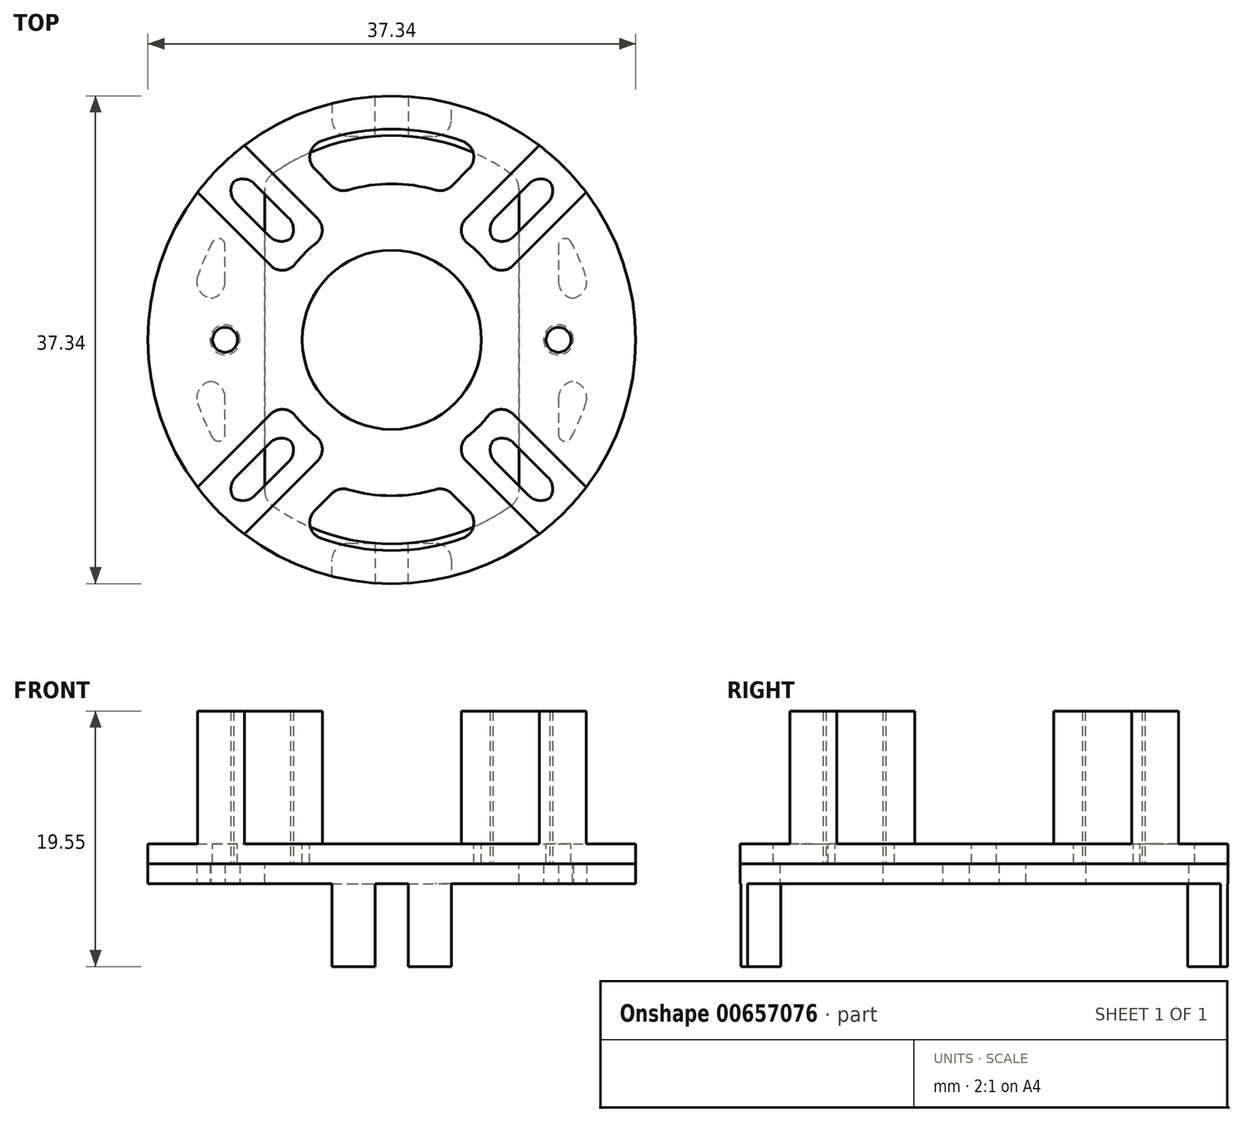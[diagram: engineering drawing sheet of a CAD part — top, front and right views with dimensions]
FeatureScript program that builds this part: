
annotation { "Feature Type Name" : "Feature", "Feature Type Description" : "" }
export const myFeature = defineFeature(function(context is Context, id is Id, definition is map)
    precondition{}
    {
        {
            var Q0;
            Q0=qCreatedBy(makeId("Top.planeOp"),FACE);
            var sketch = newSketch(context, id + "F0", { "sketchPlane" : qUnion([Q0])});
            skCircle(sketch, "E0", {"center": v(0, 0) * mm, "radius": 18.67 * mm});
            skSolve(sketch);
        }
        {
            var Q0;
            Q0=qSketchRegion(id+"F0",true);
            extrude(context, id + "F1", {"entities" : qUnion([Q0]), "depth" : 1.52 * mm, "offsetDistance" : 25.4 * mm});
        }
        {
            var Q0;
            Q0=makeQuery(id+"F1.opExtrude","CAP_FACE",FACE,{"disambiguationData":[OSD([sQuery(id+"F0.wireOp",EDGE,"E0")])],"isStart":false});
            var sketch = newSketch(context, id + "F2", { "sketchPlane" : qUnion([Q0])});
            skArc(sketch, "E1", {"start": v(-8.2, 4.6) * mm, "mid": v(-9.4, 0) * mm, "end": v(-8.2, -4.6) * mm, "construction": true});
            skArc(sketch, "E2", {"start": v(-4.6, 8.2) * mm, "mid": v(-6.65, 6.65) * mm, "end": v(-8.2, 4.6) * mm});
            skArc(sketch, "E3", {"start": v(4.6, 8.2) * mm, "mid": v(0, 9.4) * mm, "end": v(-4.6, 8.2) * mm, "construction": true});
            skArc(sketch, "E4", {"start": v(8.2, 4.6) * mm, "mid": v(6.65, 6.65) * mm, "end": v(4.6, 8.2) * mm});
            skArc(sketch, "E5", {"start": v(8.2, -4.6) * mm, "mid": v(9.4, 0) * mm, "end": v(8.2, 4.6) * mm, "construction": true});
            skArc(sketch, "E6", {"start": v(4.6, -8.2) * mm, "mid": v(6.65, -6.65) * mm, "end": v(8.2, -4.6) * mm});
            skArc(sketch, "E7", {"start": v(-4.6, -8.2) * mm, "mid": v(0, -9.4) * mm, "end": v(4.6, -8.2) * mm, "construction": true});
            skArc(sketch, "E8", {"start": v(-8.2, -4.6) * mm, "mid": v(-6.65, -6.65) * mm, "end": v(-4.6, -8.2) * mm});
            skArc(sketch, "E9", {"start": v(-14.87, -11.28) * mm, "mid": v(-13.2, -13.2) * mm, "end": v(-11.28, -14.87) * mm});
            skArc(sketch, "E10", {"start": v(-14.87, 11.28) * mm, "mid": v(-18.67, 0) * mm, "end": v(-14.87, -11.28) * mm, "construction": true});
            skArc(sketch, "E11", {"start": v(-11.28, 14.87) * mm, "mid": v(-13.2, 13.2) * mm, "end": v(-14.87, 11.28) * mm});
            skArc(sketch, "E12", {"start": v(11.28, 14.87) * mm, "mid": v(0, 18.67) * mm, "end": v(-11.28, 14.87) * mm, "construction": true});
            skArc(sketch, "E13", {"start": v(14.87, 11.28) * mm, "mid": v(13.2, 13.2) * mm, "end": v(11.28, 14.87) * mm});
            skArc(sketch, "E14", {"start": v(14.87, -11.28) * mm, "mid": v(18.67, 0) * mm, "end": v(14.87, 11.28) * mm, "construction": true});
            skArc(sketch, "E15", {"start": v(11.28, -14.87) * mm, "mid": v(13.2, -13.2) * mm, "end": v(14.87, -11.28) * mm});
            skArc(sketch, "E16", {"start": v(-11.28, -14.87) * mm, "mid": v(0, -18.67) * mm, "end": v(11.28, -14.87) * mm, "construction": true});
            skLineSegment(sketch, "E17", {"start": v(-14.87, 11.28) * mm, "end": v(-8.2, 4.6) * mm});
            skLineSegment(sketch, "E18", {"start": v(-4.6, 8.2) * mm, "end": v(-11.28, 14.87) * mm});
            skLineSegment(sketch, "E19", {"start": v(4.6, 8.2) * mm, "end": v(11.28, 14.87) * mm});
            skLineSegment(sketch, "E20", {"start": v(8.2, 4.6) * mm, "end": v(14.87, 11.28) * mm});
            skLineSegment(sketch, "E21", {"start": v(4.6, -8.2) * mm, "end": v(11.28, -14.87) * mm});
            skLineSegment(sketch, "E22", {"start": v(8.2, -4.6) * mm, "end": v(14.87, -11.28) * mm});
            skLineSegment(sketch, "E23", {"start": v(-11.28, -14.87) * mm, "end": v(-4.6, -8.2) * mm});
            skLineSegment(sketch, "E24", {"start": v(-14.87, -11.28) * mm, "end": v(-8.2, -4.6) * mm});
            skLineSegment(sketch, "E25", {"start": v(8.2, 4.6) * mm, "end": v(0, 4.6) * mm, "construction": true});
            skLineSegment(sketch, "E26", {"start": v(4.6, 8.2) * mm, "end": v(4.6, 0) * mm, "construction": true});
            skSolve(sketch);
        }
        {
            var Q0;
            Q0=qSketchRegion(id+"F2",true);
            extrude(context, id + "F3", {"entities" : qUnion([Q0]), "operationType" : NewBodyOperationType.ADD, "depth" : 10.16 * mm, "offsetDistance" : 25.4 * mm});
        }
        {
            var Q0;
            Q0=makeQuery(id+"F1.opExtrude","CAP_FACE",FACE,{"disambiguationData":[OSD([sQuery(id+"F0.wireOp",EDGE,"E0")])],"isStart":false});
            var sketch = newSketch(context, id + "F4", { "sketchPlane" : qUnion([Q0])});
            skCircle(sketch, "E27", {"center": v(0, 0) * mm, "radius": 6.86 * mm});
            skArc(sketch, "E28", {"start": v(-14.42, 7.23) * mm, "mid": v(-16.13, 0) * mm, "end": v(-14.42, -7.23) * mm, "construction": true});
            skArc(sketch, "E29", {"start": v(-14.42, -7.23) * mm, "mid": v(-11.4, -11.4) * mm, "end": v(-7.23, -14.42) * mm, "construction": true});
            skArc(sketch, "E30", {"start": v(-11.23, -4.05) * mm, "mid": v(-8.44, -8.44) * mm, "end": v(-4.05, -11.23) * mm, "construction": true});
            skArc(sketch, "E31", {"start": v(-11.23, 4.05) * mm, "mid": v(-11.94, 0) * mm, "end": v(-11.23, -4.05) * mm, "construction": true});
            skArc(sketch, "E32", {"start": v(-7.23, 14.42) * mm, "mid": v(-11.4, 11.4) * mm, "end": v(-14.42, 7.23) * mm, "construction": true});
            skArc(sketch, "E33", {"start": v(-4.05, 11.23) * mm, "mid": v(-8.44, 8.44) * mm, "end": v(-11.23, 4.05) * mm, "construction": true});
            skArc(sketch, "E34", {"start": v(4.05, 11.23) * mm, "mid": v(0, 11.94) * mm, "end": v(-4.05, 11.23) * mm});
            skArc(sketch, "E35", {"start": v(7.23, 14.42) * mm, "mid": v(0, 16.13) * mm, "end": v(-7.23, 14.42) * mm});
            skArc(sketch, "E36", {"start": v(14.42, 7.23) * mm, "mid": v(11.4, 11.4) * mm, "end": v(7.23, 14.42) * mm, "construction": true});
            skArc(sketch, "E37", {"start": v(11.23, 4.05) * mm, "mid": v(8.44, 8.44) * mm, "end": v(4.05, 11.23) * mm, "construction": true});
            skArc(sketch, "E38", {"start": v(11.23, -4.05) * mm, "mid": v(11.94, 0) * mm, "end": v(11.23, 4.05) * mm, "construction": true});
            skArc(sketch, "E39", {"start": v(14.42, -7.23) * mm, "mid": v(16.13, 0) * mm, "end": v(14.42, 7.23) * mm, "construction": true});
            skArc(sketch, "E40", {"start": v(7.23, -14.42) * mm, "mid": v(11.4, -11.4) * mm, "end": v(14.42, -7.23) * mm, "construction": true});
            skArc(sketch, "E41", {"start": v(4.05, -11.23) * mm, "mid": v(8.44, -8.44) * mm, "end": v(11.23, -4.05) * mm, "construction": true});
            skArc(sketch, "E42", {"start": v(-4.05, -11.23) * mm, "mid": v(0, -11.94) * mm, "end": v(4.05, -11.23) * mm});
            skArc(sketch, "E43", {"start": v(-7.23, -14.42) * mm, "mid": v(0, -16.13) * mm, "end": v(7.23, -14.42) * mm});
            skLineSegment(sketch, "E44", {"start": v(-14.42, -7.23) * mm, "end": v(-11.23, -4.05) * mm, "construction": true});
            skLineSegment(sketch, "E45", {"start": v(-14.42, 7.23) * mm, "end": v(-11.23, 4.05) * mm, "construction": true});
            skLineSegment(sketch, "E46", {"start": v(-7.23, 14.42) * mm, "end": v(-4.05, 11.23) * mm});
            skLineSegment(sketch, "E47", {"start": v(4.05, 11.23) * mm, "end": v(7.23, 14.42) * mm});
            skLineSegment(sketch, "E48", {"start": v(11.23, 4.05) * mm, "end": v(14.42, 7.23) * mm, "construction": true});
            skLineSegment(sketch, "E49", {"start": v(11.23, -4.05) * mm, "end": v(14.42, -7.23) * mm, "construction": true});
            skLineSegment(sketch, "E50", {"start": v(4.05, -11.23) * mm, "end": v(7.23, -14.42) * mm});
            skLineSegment(sketch, "E51", {"start": v(-7.23, -14.42) * mm, "end": v(-4.05, -11.23) * mm});
            skSolve(sketch);
        }
        {
            var Q0;
            Q0=qSketchRegion(id+"F4",true);
            var Q1;
            Q1=makeQuery(id+"F1.opExtrude","SWEPT_BODY",BODY,{"disambiguationData":[OSD([sQuery(id+"F0.wireOp",EDGE,"E0")])]});
            extrude(context, id + "F5", {"entities" : qUnion([Q0]), "operationType" : NewBodyOperationType.REMOVE, "endBound" : BoundingType.UP_TO_BODY, "oppositeDirection" : true, "depth" : 25.4 * mm, "endBoundEntityBody" : qUnion([Q1]), "offsetDistance" : 25.4 * mm});
        }
        {
            var Q0;
            Q0=makeQuery(id+"F5.boolean.opBoolean","COPY",EDGE,{"derivedFrom":makeQuery(id+"F5.opExtrude","SWEPT_EDGE",EDGE,{"disambiguationData":[OSD([sQuery(id+"F4.wireOp",EDGE,"E28"),sQuery(id+"F4.wireOp",EDGE,"E45")])]})});
            var Q1;
            Q1=makeQuery(id+"F5.boolean.opBoolean","COPY",EDGE,{"derivedFrom":makeQuery(id+"F5.opExtrude","SWEPT_EDGE",EDGE,{"disambiguationData":[OSD([sQuery(id+"F4.wireOp",EDGE,"E31"),sQuery(id+"F4.wireOp",EDGE,"E45")])]})});
            var Q2;
            Q2=makeQuery(id+"F5.boolean.opBoolean","COPY",EDGE,{"derivedFrom":makeQuery(id+"F5.opExtrude","SWEPT_EDGE",EDGE,{"disambiguationData":[OSD([sQuery(id+"F4.wireOp",EDGE,"E31"),sQuery(id+"F4.wireOp",EDGE,"E44")])]})});
            var Q3;
            Q3=makeQuery(id+"F5.boolean.opBoolean","COPY",EDGE,{"derivedFrom":makeQuery(id+"F5.opExtrude","SWEPT_EDGE",EDGE,{"disambiguationData":[OSD([sQuery(id+"F4.wireOp",EDGE,"E28"),sQuery(id+"F4.wireOp",EDGE,"E44")])]})});
            var Q4;
            Q4=makeQuery(id+"F5.boolean.opBoolean","COPY",EDGE,{"derivedFrom":makeQuery(id+"F5.opExtrude","SWEPT_EDGE",EDGE,{"disambiguationData":[OSD([sQuery(id+"F4.wireOp",EDGE,"E34"),sQuery(id+"F4.wireOp",EDGE,"E46")])]})});
            var Q5;
            Q5=makeQuery(id+"F5.boolean.opBoolean","COPY",EDGE,{"derivedFrom":makeQuery(id+"F5.opExtrude","SWEPT_EDGE",EDGE,{"disambiguationData":[OSD([sQuery(id+"F4.wireOp",EDGE,"E34"),sQuery(id+"F4.wireOp",EDGE,"E47")])]})});
            var Q6;
            Q6=makeQuery(id+"F5.boolean.opBoolean","COPY",EDGE,{"derivedFrom":makeQuery(id+"F5.opExtrude","SWEPT_EDGE",EDGE,{"disambiguationData":[OSD([sQuery(id+"F4.wireOp",EDGE,"E35"),sQuery(id+"F4.wireOp",EDGE,"E46")])]})});
            var Q7;
            Q7=makeQuery(id+"F5.boolean.opBoolean","COPY",EDGE,{"derivedFrom":makeQuery(id+"F5.opExtrude","SWEPT_EDGE",EDGE,{"disambiguationData":[OSD([sQuery(id+"F4.wireOp",EDGE,"E35"),sQuery(id+"F4.wireOp",EDGE,"E47")])]})});
            var Q8;
            Q8=makeQuery(id+"F5.boolean.opBoolean","COPY",EDGE,{"derivedFrom":makeQuery(id+"F5.opExtrude","SWEPT_EDGE",EDGE,{"disambiguationData":[OSD([sQuery(id+"F4.wireOp",EDGE,"E42"),sQuery(id+"F4.wireOp",EDGE,"E50")])]})});
            var Q9;
            Q9=makeQuery(id+"F5.boolean.opBoolean","COPY",EDGE,{"derivedFrom":makeQuery(id+"F5.opExtrude","SWEPT_EDGE",EDGE,{"disambiguationData":[OSD([sQuery(id+"F4.wireOp",EDGE,"E42"),sQuery(id+"F4.wireOp",EDGE,"E51")])]})});
            var Q10;
            Q10=makeQuery(id+"F5.boolean.opBoolean","COPY",EDGE,{"derivedFrom":makeQuery(id+"F5.opExtrude","SWEPT_EDGE",EDGE,{"disambiguationData":[OSD([sQuery(id+"F4.wireOp",EDGE,"E39"),sQuery(id+"F4.wireOp",EDGE,"E48")])]})});
            var Q11;
            Q11=makeQuery(id+"F5.boolean.opBoolean","COPY",EDGE,{"derivedFrom":makeQuery(id+"F5.opExtrude","SWEPT_EDGE",EDGE,{"disambiguationData":[OSD([sQuery(id+"F4.wireOp",EDGE,"E43"),sQuery(id+"F4.wireOp",EDGE,"E50")])]})});
            var Q12;
            Q12=makeQuery(id+"F5.boolean.opBoolean","COPY",EDGE,{"derivedFrom":makeQuery(id+"F5.opExtrude","SWEPT_EDGE",EDGE,{"disambiguationData":[OSD([sQuery(id+"F4.wireOp",EDGE,"E43"),sQuery(id+"F4.wireOp",EDGE,"E51")])]})});
            var Q13;
            Q13=makeQuery(id+"F5.boolean.opBoolean","COPY",EDGE,{"derivedFrom":makeQuery(id+"F5.opExtrude","SWEPT_EDGE",EDGE,{"disambiguationData":[OSD([sQuery(id+"F4.wireOp",EDGE,"E38"),sQuery(id+"F4.wireOp",EDGE,"E48")])]})});
            var Q14;
            Q14=makeQuery(id+"F5.boolean.opBoolean","COPY",EDGE,{"derivedFrom":makeQuery(id+"F5.opExtrude","SWEPT_EDGE",EDGE,{"disambiguationData":[OSD([sQuery(id+"F4.wireOp",EDGE,"E38"),sQuery(id+"F4.wireOp",EDGE,"E49")])]})});
            var Q15;
            Q15=makeQuery(id+"F5.boolean.opBoolean","COPY",EDGE,{"derivedFrom":makeQuery(id+"F5.opExtrude","SWEPT_EDGE",EDGE,{"disambiguationData":[OSD([sQuery(id+"F4.wireOp",EDGE,"E39"),sQuery(id+"F4.wireOp",EDGE,"E49")])]})});
            var Q16;
            Q16=makeQuery(id+"F3.opExtrude","SWEPT_EDGE",EDGE,{"disambiguationData":[OSD([sQuery(id+"F2.wireOp",EDGE,"E8"),sQuery(id+"F2.wireOp",EDGE,"E23")])]});
            var Q17;
            Q17=makeQuery(id+"F3.opExtrude","SWEPT_EDGE",EDGE,{"disambiguationData":[OSD([sQuery(id+"F2.wireOp",EDGE,"E8"),sQuery(id+"F2.wireOp",EDGE,"E24")])]});
            var Q18;
            Q18=makeQuery(id+"F3.opExtrude","SWEPT_EDGE",EDGE,{"disambiguationData":[OSD([sQuery(id+"F2.wireOp",EDGE,"E2"),sQuery(id+"F2.wireOp",EDGE,"E17")])]});
            var Q19;
            Q19=makeQuery(id+"F3.opExtrude","SWEPT_EDGE",EDGE,{"disambiguationData":[OSD([sQuery(id+"F2.wireOp",EDGE,"E2"),sQuery(id+"F2.wireOp",EDGE,"E18")])]});
            var Q20;
            Q20=makeQuery(id+"F3.opExtrude","SWEPT_EDGE",EDGE,{"disambiguationData":[OSD([sQuery(id+"F2.wireOp",EDGE,"E6"),sQuery(id+"F2.wireOp",EDGE,"E22")])]});
            var Q21;
            Q21=makeQuery(id+"F3.opExtrude","SWEPT_EDGE",EDGE,{"disambiguationData":[OSD([sQuery(id+"F2.wireOp",EDGE,"E4"),sQuery(id+"F2.wireOp",EDGE,"E20")])]});
            var Q22;
            Q22=makeQuery(id+"F3.opExtrude","SWEPT_EDGE",EDGE,{"disambiguationData":[OSD([sQuery(id+"F2.wireOp",EDGE,"E4"),sQuery(id+"F2.wireOp",EDGE,"E19")])]});
            var Q23;
            Q23=makeQuery(id+"F3.opExtrude","SWEPT_EDGE",EDGE,{"disambiguationData":[OSD([sQuery(id+"F2.wireOp",EDGE,"E6"),sQuery(id+"F2.wireOp",EDGE,"E21")])]});
            fillet(context, id + "F6", {"entities" : qUnion([Q0, Q1, Q2, Q3, Q4, Q5, Q6, Q7, Q8, Q9, Q10, Q11, Q12, Q13, Q14, Q15, Q16, Q17, Q18, Q19, Q20, Q21, Q22, Q23]), "radius" : 1.27 * mm, "tangentPropagation" : true, "allowEdgeOverflow" : false});
        }
        {
            var Q0;
            Q0=makeQuery(id+"F3.opExtrude","CAP_FACE",FACE,{"disambiguationData":[OSD([sQuery(id+"F2.wireOp",EDGE,"E8"),sQuery(id+"F2.wireOp",EDGE,"E9"),sQuery(id+"F2.wireOp",EDGE,"E23"),sQuery(id+"F2.wireOp",EDGE,"E24")])],"isStart":false});
            var Q1;
            Q1=makeQuery(id+"F3.opExtrude","CAP_FACE",FACE,{"disambiguationData":[OSD([sQuery(id+"F2.wireOp",EDGE,"E2"),sQuery(id+"F2.wireOp",EDGE,"E11"),sQuery(id+"F2.wireOp",EDGE,"E17"),sQuery(id+"F2.wireOp",EDGE,"E18")])],"isStart":false});
            var Q2;
            Q2=makeQuery(id+"F3.opExtrude","CAP_FACE",FACE,{"disambiguationData":[OSD([sQuery(id+"F2.wireOp",EDGE,"E6"),sQuery(id+"F2.wireOp",EDGE,"E15"),sQuery(id+"F2.wireOp",EDGE,"E21"),sQuery(id+"F2.wireOp",EDGE,"E22")])],"isStart":false});
            var Q3;
            Q3=makeQuery(id+"F3.opExtrude","CAP_FACE",FACE,{"disambiguationData":[OSD([sQuery(id+"F2.wireOp",EDGE,"E4"),sQuery(id+"F2.wireOp",EDGE,"E13"),sQuery(id+"F2.wireOp",EDGE,"E19"),sQuery(id+"F2.wireOp",EDGE,"E20")])],"isStart":false});
            shell(context, id + "F7", {"entities" : qUnion([Q0, Q1, Q2, Q3]), "thickness" : 1.52 * mm});
        }
        {
            var Q0;
            Q0=makeQuery(id+"F7.opShell","OFFSET_FACE",FACE,{"disambiguationData":[OSD([sQuery(id+"F0.wireOp",EDGE,"E0")]),OD(3.0)]});
            var Q1;
            Q1=makeQuery(id+"F7.opShell","OFFSET_FACE",FACE,{"disambiguationData":[OSD([sQuery(id+"F0.wireOp",EDGE,"E0")]),OD(0.0)]});
            var Q2;
            Q2=makeQuery(id+"F7.opShell","OFFSET_FACE",FACE,{"disambiguationData":[OSD([sQuery(id+"F0.wireOp",EDGE,"E0")]),OD(2.0)]});
            var Q3;
            Q3=makeQuery(id+"F7.opShell","OFFSET_FACE",FACE,{"disambiguationData":[OSD([sQuery(id+"F0.wireOp",EDGE,"E0")]),OD(1.0)]});
            var Q4;
            Q4=makeQuery(id+"F1.opExtrude","CAP_FACE",FACE,{"disambiguationData":[OSD([sQuery(id+"F0.wireOp",EDGE,"E0")])],"isStart":true});
            extrude(context, id + "F8", {"entities" : qUnion([Q0, Q1, Q2, Q3]), "operationType" : NewBodyOperationType.REMOVE, "endBound" : BoundingType.UP_TO_SURFACE, "oppositeDirection" : true, "depth" : 25.4 * mm, "endBoundEntityFace" : qUnion([Q4]), "offsetDistance" : 25.4 * mm});
        }
        {
            var Q0;
            Q0=makeQuery(id+"F3.opExtrude","CAP_EDGE",EDGE,{"disambiguationData":[OSD([sQuery(id+"F2.wireOp",EDGE,"E4")])],"isStart":true});
            var Q1;
            Q1=makeQuery(id+"F3.opExtrude","CAP_EDGE",EDGE,{"disambiguationData":[OSD([sQuery(id+"F2.wireOp",EDGE,"E2")])],"isStart":true});
            var Q2;
            Q2=makeQuery(id+"F3.opExtrude","CAP_EDGE",EDGE,{"disambiguationData":[OSD([sQuery(id+"F2.wireOp",EDGE,"E8")])],"isStart":true});
            var Q3;
            Q3=makeQuery(id+"F3.opExtrude","CAP_EDGE",EDGE,{"disambiguationData":[OSD([sQuery(id+"F2.wireOp",EDGE,"E6")])],"isStart":true});
            var Q4;
            {var subQ0=sQuery(id+"F2.wireOp",EDGE,"E17");var subQ1=sQuery(id+"F2.wireOp",EDGE,"E2");Q4=makeQuery(id+"F8.boolean.opBoolean","MERGE",EDGE,{"derivedFrom":[makeQuery(id+"F7.opShell","OFFSET_EDGE",EDGE,{"disambiguationData":[OSD([subQ1,subQ0])]}),makeQuery(id+"F8.opExtrude","SWEPT_EDGE",EDGE,{"disambiguationData":[OSD([sQuery(id+"F0.wireOp",EDGE,"E0"),subQ1,subQ0])]})]});}
            var Q5;
            {var subQ0=sQuery(id+"F2.wireOp",EDGE,"E18");var subQ1=sQuery(id+"F2.wireOp",EDGE,"E2");Q5=makeQuery(id+"F8.boolean.opBoolean","MERGE",EDGE,{"derivedFrom":[makeQuery(id+"F7.opShell","OFFSET_EDGE",EDGE,{"disambiguationData":[OSD([subQ1,subQ0])]}),makeQuery(id+"F8.opExtrude","SWEPT_EDGE",EDGE,{"disambiguationData":[OSD([sQuery(id+"F0.wireOp",EDGE,"E0"),subQ1,subQ0])]})]});}
            var Q6;
            {var subQ0=sQuery(id+"F2.wireOp",EDGE,"E18");var subQ1=sQuery(id+"F2.wireOp",EDGE,"E11");var subQ2=sQuery(id+"F0.wireOp",EDGE,"E0");Q6=makeQuery(id+"F8.boolean.opBoolean","MERGE",EDGE,{"derivedFrom":[makeQuery(id+"F7.opShell","OFFSET_EDGE",EDGE,{"disambiguationData":[OSD([subQ2,subQ1,subQ0])]}),makeQuery(id+"F8.opExtrude","SWEPT_EDGE",EDGE,{"disambiguationData":[OSD([subQ2,sQuery(id+"F2.wireOp",EDGE,"E9"),subQ1,sQuery(id+"F2.wireOp",EDGE,"E13"),sQuery(id+"F2.wireOp",EDGE,"E15"),subQ0])]})]});}
            var Q7;
            {var subQ0=sQuery(id+"F2.wireOp",EDGE,"E17");var subQ1=sQuery(id+"F2.wireOp",EDGE,"E11");var subQ2=sQuery(id+"F0.wireOp",EDGE,"E0");Q7=makeQuery(id+"F8.boolean.opBoolean","MERGE",EDGE,{"derivedFrom":[makeQuery(id+"F7.opShell","OFFSET_EDGE",EDGE,{"disambiguationData":[OSD([subQ2,subQ1,subQ0])]}),makeQuery(id+"F8.opExtrude","SWEPT_EDGE",EDGE,{"disambiguationData":[OSD([subQ2,sQuery(id+"F2.wireOp",EDGE,"E9"),subQ1,sQuery(id+"F2.wireOp",EDGE,"E13"),sQuery(id+"F2.wireOp",EDGE,"E15"),subQ0])]})]});}
            var Q8;
            {var subQ0=sQuery(id+"F2.wireOp",EDGE,"E24");var subQ1=sQuery(id+"F2.wireOp",EDGE,"E8");Q8=makeQuery(id+"F8.boolean.opBoolean","MERGE",EDGE,{"derivedFrom":[makeQuery(id+"F7.opShell","OFFSET_EDGE",EDGE,{"disambiguationData":[OSD([subQ1,subQ0])]}),makeQuery(id+"F8.opExtrude","SWEPT_EDGE",EDGE,{"disambiguationData":[OSD([sQuery(id+"F0.wireOp",EDGE,"E0"),subQ1,subQ0])]})]});}
            var Q9;
            {var subQ0=sQuery(id+"F2.wireOp",EDGE,"E24");var subQ1=sQuery(id+"F2.wireOp",EDGE,"E9");var subQ2=sQuery(id+"F0.wireOp",EDGE,"E0");Q9=makeQuery(id+"F8.boolean.opBoolean","MERGE",EDGE,{"derivedFrom":[makeQuery(id+"F7.opShell","OFFSET_EDGE",EDGE,{"disambiguationData":[OSD([subQ2,subQ1,subQ0])]}),makeQuery(id+"F8.opExtrude","SWEPT_EDGE",EDGE,{"disambiguationData":[OSD([subQ2,subQ1,sQuery(id+"F2.wireOp",EDGE,"E11"),sQuery(id+"F2.wireOp",EDGE,"E13"),sQuery(id+"F2.wireOp",EDGE,"E15"),subQ0])]})]});}
            var Q10;
            {var subQ0=sQuery(id+"F2.wireOp",EDGE,"E23");var subQ1=sQuery(id+"F2.wireOp",EDGE,"E9");var subQ2=sQuery(id+"F0.wireOp",EDGE,"E0");Q10=makeQuery(id+"F8.boolean.opBoolean","MERGE",EDGE,{"derivedFrom":[makeQuery(id+"F7.opShell","OFFSET_EDGE",EDGE,{"disambiguationData":[OSD([subQ2,subQ1,subQ0])]}),makeQuery(id+"F8.opExtrude","SWEPT_EDGE",EDGE,{"disambiguationData":[OSD([subQ2,subQ1,sQuery(id+"F2.wireOp",EDGE,"E11"),sQuery(id+"F2.wireOp",EDGE,"E13"),sQuery(id+"F2.wireOp",EDGE,"E15"),subQ0])]})]});}
            var Q11;
            {var subQ0=sQuery(id+"F2.wireOp",EDGE,"E23");var subQ1=sQuery(id+"F2.wireOp",EDGE,"E8");Q11=makeQuery(id+"F8.boolean.opBoolean","MERGE",EDGE,{"derivedFrom":[makeQuery(id+"F7.opShell","OFFSET_EDGE",EDGE,{"disambiguationData":[OSD([subQ1,subQ0])]}),makeQuery(id+"F8.opExtrude","SWEPT_EDGE",EDGE,{"disambiguationData":[OSD([sQuery(id+"F0.wireOp",EDGE,"E0"),subQ1,subQ0])]})]});}
            var Q12;
            {var subQ0=sQuery(id+"F2.wireOp",EDGE,"E20");var subQ1=sQuery(id+"F2.wireOp",EDGE,"E13");var subQ2=sQuery(id+"F0.wireOp",EDGE,"E0");Q12=makeQuery(id+"F8.boolean.opBoolean","MERGE",EDGE,{"derivedFrom":[makeQuery(id+"F7.opShell","OFFSET_EDGE",EDGE,{"disambiguationData":[OSD([subQ2,subQ1,subQ0])]}),makeQuery(id+"F8.opExtrude","SWEPT_EDGE",EDGE,{"disambiguationData":[OSD([subQ2,sQuery(id+"F2.wireOp",EDGE,"E9"),sQuery(id+"F2.wireOp",EDGE,"E11"),subQ1,sQuery(id+"F2.wireOp",EDGE,"E15"),subQ0])]})]});}
            var Q13;
            {var subQ0=sQuery(id+"F2.wireOp",EDGE,"E22");var subQ1=sQuery(id+"F2.wireOp",EDGE,"E15");var subQ2=sQuery(id+"F0.wireOp",EDGE,"E0");Q13=makeQuery(id+"F8.boolean.opBoolean","MERGE",EDGE,{"derivedFrom":[makeQuery(id+"F7.opShell","OFFSET_EDGE",EDGE,{"disambiguationData":[OSD([subQ2,subQ1,subQ0])]}),makeQuery(id+"F8.opExtrude","SWEPT_EDGE",EDGE,{"disambiguationData":[OSD([subQ2,sQuery(id+"F2.wireOp",EDGE,"E9"),sQuery(id+"F2.wireOp",EDGE,"E11"),sQuery(id+"F2.wireOp",EDGE,"E13"),subQ1,subQ0])]})]});}
            var Q14;
            {var subQ0=sQuery(id+"F2.wireOp",EDGE,"E19");var subQ1=sQuery(id+"F2.wireOp",EDGE,"E4");Q14=makeQuery(id+"F8.boolean.opBoolean","MERGE",EDGE,{"derivedFrom":[makeQuery(id+"F7.opShell","OFFSET_EDGE",EDGE,{"disambiguationData":[OSD([subQ1,subQ0])]}),makeQuery(id+"F8.opExtrude","SWEPT_EDGE",EDGE,{"disambiguationData":[OSD([sQuery(id+"F0.wireOp",EDGE,"E0"),subQ1,subQ0])]})]});}
            var Q15;
            {var subQ0=sQuery(id+"F2.wireOp",EDGE,"E21");var subQ1=sQuery(id+"F2.wireOp",EDGE,"E6");Q15=makeQuery(id+"F8.boolean.opBoolean","MERGE",EDGE,{"derivedFrom":[makeQuery(id+"F7.opShell","OFFSET_EDGE",EDGE,{"disambiguationData":[OSD([subQ1,subQ0])]}),makeQuery(id+"F8.opExtrude","SWEPT_EDGE",EDGE,{"disambiguationData":[OSD([sQuery(id+"F0.wireOp",EDGE,"E0"),subQ1,subQ0])]})]});}
            var Q16;
            {var subQ0=sQuery(id+"F2.wireOp",EDGE,"E19");var subQ1=sQuery(id+"F2.wireOp",EDGE,"E13");var subQ2=sQuery(id+"F0.wireOp",EDGE,"E0");Q16=makeQuery(id+"F8.boolean.opBoolean","MERGE",EDGE,{"derivedFrom":[makeQuery(id+"F7.opShell","OFFSET_EDGE",EDGE,{"disambiguationData":[OSD([subQ2,subQ1,subQ0])]}),makeQuery(id+"F8.opExtrude","SWEPT_EDGE",EDGE,{"disambiguationData":[OSD([subQ2,sQuery(id+"F2.wireOp",EDGE,"E9"),sQuery(id+"F2.wireOp",EDGE,"E11"),subQ1,sQuery(id+"F2.wireOp",EDGE,"E15"),subQ0])]})]});}
            var Q17;
            {var subQ0=sQuery(id+"F2.wireOp",EDGE,"E22");var subQ1=sQuery(id+"F2.wireOp",EDGE,"E6");Q17=makeQuery(id+"F8.boolean.opBoolean","MERGE",EDGE,{"derivedFrom":[makeQuery(id+"F7.opShell","OFFSET_EDGE",EDGE,{"disambiguationData":[OSD([subQ1,subQ0])]}),makeQuery(id+"F8.opExtrude","SWEPT_EDGE",EDGE,{"disambiguationData":[OSD([sQuery(id+"F0.wireOp",EDGE,"E0"),subQ1,subQ0])]})]});}
            var Q18;
            {var subQ0=sQuery(id+"F2.wireOp",EDGE,"E21");var subQ1=sQuery(id+"F2.wireOp",EDGE,"E15");var subQ2=sQuery(id+"F0.wireOp",EDGE,"E0");Q18=makeQuery(id+"F8.boolean.opBoolean","MERGE",EDGE,{"derivedFrom":[makeQuery(id+"F7.opShell","OFFSET_EDGE",EDGE,{"disambiguationData":[OSD([subQ2,subQ1,subQ0])]}),makeQuery(id+"F8.opExtrude","SWEPT_EDGE",EDGE,{"disambiguationData":[OSD([subQ2,sQuery(id+"F2.wireOp",EDGE,"E9"),sQuery(id+"F2.wireOp",EDGE,"E11"),sQuery(id+"F2.wireOp",EDGE,"E13"),subQ1,subQ0])]})]});}
            var Q19;
            {var subQ0=sQuery(id+"F2.wireOp",EDGE,"E20");var subQ1=sQuery(id+"F2.wireOp",EDGE,"E4");Q19=makeQuery(id+"F8.boolean.opBoolean","MERGE",EDGE,{"derivedFrom":[makeQuery(id+"F7.opShell","OFFSET_EDGE",EDGE,{"disambiguationData":[OSD([subQ1,subQ0])]}),makeQuery(id+"F8.opExtrude","SWEPT_EDGE",EDGE,{"disambiguationData":[OSD([sQuery(id+"F0.wireOp",EDGE,"E0"),subQ1,subQ0])]})]});}
            fillet(context, id + "F9", {"entities" : qUnion([Q0, Q1, Q2, Q3, Q4, Q5, Q6, Q7, Q8, Q9, Q10, Q11, Q12, Q13, Q14, Q15, Q16, Q17, Q18, Q19]), "radius" : 1.27 * mm, "tangentPropagation" : true, "allowEdgeOverflow" : false});
        }
        {
            var Q0;
            Q0=makeQuery(id+"F1.opExtrude","CAP_FACE",FACE,{"disambiguationData":[OSD([sQuery(id+"F0.wireOp",EDGE,"E0")])],"isStart":false});
            var sketch = newSketch(context, id + "F10", { "sketchPlane" : qUnion([Q0])});
            skCircle(sketch, "E52", {"center": v(-12.76, 0) * mm, "radius": 0.95 * mm});
            skCircle(sketch, "E53", {"center": v(12.76, 0) * mm, "radius": 0.95 * mm});
            skLineSegment(sketch, "E54", {"start": v(-12.76, 0) * mm, "end": v(-18.67, 0) * mm, "construction": true});
            skLineSegment(sketch, "E55", {"start": v(-12.76, 0) * mm, "end": v(0, 0) * mm, "construction": true});
            skLineSegment(sketch, "E56", {"start": v(0, 0) * mm, "end": v(12.76, 0) * mm, "construction": true});
            skLineSegment(sketch, "E57", {"start": v(-12.76, 0) * mm, "end": v(-6.86, 0) * mm, "construction": true});
            skSolve(sketch);
        }
        {
            var Q0;
            Q0 = qSketchRegion(id + "F10", true);
            var Q1;
            Q1=makeQuery(id+"F1.opExtrude","CAP_FACE",FACE,{"disambiguationData":[OSD([sQuery(id+"F0.wireOp",EDGE,"E0")])],"isStart":true});
            extrude(context, id + "F11", {"entities" : qUnion([Q0]), "operationType" : NewBodyOperationType.REMOVE, "endBound" : BoundingType.UP_TO_SURFACE, "oppositeDirection" : true, "depth" : 25.4 * mm, "endBoundEntityFace" : qUnion([Q1]), "offsetDistance" : 25.4 * mm});
        }
        {
            var Q0;
            Q0=makeQuery(id+"F1.opExtrude","CAP_FACE",FACE,{"disambiguationData":[OSD([sQuery(id+"F0.wireOp",EDGE,"E0")])],"isStart":true});
            var sketch = newSketch(context, id + "F12", { "sketchPlane" : qUnion([Q0])});
            skCircle(sketch, "E58", {"center": v(0, 0) * mm, "radius": 18.67 * mm});
            skSolve(sketch);
        }
        {
            var Q0;
            Q0 = qSketchRegion(id + "F12", true);
            extrude(context, id + "F13", {"entities" : qUnion([Q0]), "depth" : 1.52 * mm, "offsetDistance" : 25.4 * mm});
        }
        {
            var Q0;
            Q0=makeQuery(id+"F13.opExtrude","CAP_FACE",FACE,{"disambiguationData":[OSD([sQuery(id+"F12.wireOp",EDGE,"E58")])],"isStart":false});
            var sketch = newSketch(context, id + "F14", { "sketchPlane" : qUnion([Q0])});
            skCircle(sketch, "E59", {"center": v(-12.76, 0) * mm, "radius": 1.14 * mm});
            skCircle(sketch, "E60", {"center": v(12.76, 0) * mm, "radius": 1.14 * mm});
            skSolve(sketch);
        }
        {
            var Q0;
            Q0 = qSketchRegion(id + "F14", true);
            var Q1;
            Q1=makeQuery(id+"F13.opExtrude","CAP_FACE",FACE,{"disambiguationData":[OSD([sQuery(id+"F12.wireOp",EDGE,"E58")])],"isStart":true});
            extrude(context, id + "F15", {"entities" : qUnion([Q0]), "operationType" : NewBodyOperationType.REMOVE, "endBound" : BoundingType.UP_TO_SURFACE, "oppositeDirection" : true, "depth" : 25.4 * mm, "endBoundEntityFace" : qUnion([Q1]), "offsetDistance" : 25.4 * mm});
        }
        {
            var Q0;
            Q0=makeQuery(id+"F13.opExtrude","CAP_FACE",FACE,{"disambiguationData":[OSD([sQuery(id+"F12.wireOp",EDGE,"E58")])],"isStart":false});
            var sketch = newSketch(context, id + "F16", { "sketchPlane" : qUnion([Q0])});
            skLineSegment(sketch, "E61", {"start": v(-4.57, 18.1) * mm, "end": v(-4.57, 15.58) * mm});
            skLineSegment(sketch, "E62", {"start": v(-4.57, 15.58) * mm, "end": v(-1.27, 15.58) * mm});
            skLineSegment(sketch, "E63", {"start": v(-1.27, 15.58) * mm, "end": v(-1.27, 18.63) * mm});
            skLineSegment(sketch, "E64", {"start": v(1.27, 18.63) * mm, "end": v(1.27, 15.58) * mm});
            skLineSegment(sketch, "E65", {"start": v(1.27, 15.58) * mm, "end": v(4.57, 15.58) * mm});
            skLineSegment(sketch, "E66", {"start": v(4.57, 15.58) * mm, "end": v(4.57, 18.1) * mm});
            skArc(sketch, "E67", {"start": v(-1.27, 18.63) * mm, "mid": v(-2.93, 18.44) * mm, "end": v(-4.57, 18.1) * mm});
            skArc(sketch, "E68", {"start": v(4.57, 18.1) * mm, "mid": v(2.93, 18.44) * mm, "end": v(1.27, 18.63) * mm});
            skLineSegment(sketch, "E69", {"start": v(-4.57, -18.1) * mm, "end": v(-4.57, -15.58) * mm});
            skLineSegment(sketch, "E70", {"start": v(-4.57, -15.58) * mm, "end": v(-1.27, -15.58) * mm});
            skLineSegment(sketch, "E71", {"start": v(-1.27, -15.58) * mm, "end": v(-1.27, -18.63) * mm});
            skLineSegment(sketch, "E72", {"start": v(1.27, -18.63) * mm, "end": v(1.27, -15.58) * mm});
            skLineSegment(sketch, "E73", {"start": v(1.27, -15.58) * mm, "end": v(4.57, -15.58) * mm});
            skLineSegment(sketch, "E74", {"start": v(4.57, -15.58) * mm, "end": v(4.57, -18.1) * mm});
            skArc(sketch, "E75", {"start": v(-4.57, -18.1) * mm, "mid": v(-2.93, -18.44) * mm, "end": v(-1.27, -18.63) * mm});
            skArc(sketch, "E76", {"start": v(1.27, -18.63) * mm, "mid": v(2.93, -18.44) * mm, "end": v(4.57, -18.1) * mm});
            skLineSegment(sketch, "E77", {"start": v(1.27, 15.58) * mm, "end": v(-1.27, 15.58) * mm, "construction": true});
            skPoint(sketch, "E78", {"position": v(0, 15.58) * mm});
            skSolve(sketch);
        }
        {
            var Q0;
            Q0 = qSketchRegion(id + "F16", true);
            extrude(context, id + "F17", {"entities" : qUnion([Q0]), "operationType" : NewBodyOperationType.ADD, "depth" : 6.35 * mm, "offsetDistance" : 25.4 * mm});
        }
        {
            var Q0;
            Q0=makeQuery(id+"F13.opExtrude","CAP_FACE",FACE,{"disambiguationData":[OSD([sQuery(id+"F12.wireOp",EDGE,"E58")])],"isStart":false});
            var sketch = newSketch(context, id + "F18", { "sketchPlane" : qUnion([Q0])});
            skArc(sketch, "E79", {"start": v(-12.76, 9.02) * mm, "mid": v(-14.33, 6.23) * mm, "end": v(-15.3, 3.17) * mm});
            skArc(sketch, "E80", {"start": v(-15.3, 3.17) * mm, "mid": v(-15.63, 0) * mm, "end": v(-15.3, -3.17) * mm, "construction": true});
            skArc(sketch, "E81", {"start": v(-15.3, -3.17) * mm, "mid": v(-14.33, -6.23) * mm, "end": v(-12.76, -9.02) * mm});
            skArc(sketch, "E82", {"start": v(-12.76, -9.02) * mm, "mid": v(-11.36, -10.74) * mm, "end": v(-9.72, -12.24) * mm, "construction": true});
            skArc(sketch, "E83", {"start": v(12.76, -9.02) * mm, "mid": v(14.33, -6.23) * mm, "end": v(15.3, -3.17) * mm});
            skArc(sketch, "E84", {"start": v(15.3, -3.18) * mm, "mid": v(15.63, 0) * mm, "end": v(15.3, 3.17) * mm, "construction": true});
            skArc(sketch, "E85", {"start": v(15.3, 3.17) * mm, "mid": v(14.33, 6.23) * mm, "end": v(12.76, 9.02) * mm});
            skArc(sketch, "E86", {"start": v(12.76, 9.02) * mm, "mid": v(11.36, 10.74) * mm, "end": v(9.72, 12.24) * mm, "construction": true});
            skLineSegment(sketch, "E87", {"start": v(-12.76, 9.02) * mm, "end": v(-12.76, 3.17) * mm});
            skLineSegment(sketch, "E88", {"start": v(-12.76, 3.17) * mm, "end": v(-15.3, 3.17) * mm});
            skLineSegment(sketch, "E89", {"start": v(-15.3, -3.17) * mm, "end": v(-12.76, -3.17) * mm});
            skLineSegment(sketch, "E90", {"start": v(-12.76, -3.17) * mm, "end": v(-12.76, -9.02) * mm});
            skLineSegment(sketch, "E91", {"start": v(12.76, -9.02) * mm, "end": v(12.76, -3.17) * mm});
            skLineSegment(sketch, "E92", {"start": v(12.76, -3.18) * mm, "end": v(15.3, -3.18) * mm});
            skLineSegment(sketch, "E93", {"start": v(15.3, 3.17) * mm, "end": v(12.76, 3.17) * mm});
            skLineSegment(sketch, "E94", {"start": v(12.76, 3.17) * mm, "end": v(12.76, 9.02) * mm});
            skArc(sketch, "E95", {"start": v(-9.72, 12.24) * mm, "mid": v(-11.36, 10.74) * mm, "end": v(-12.76, 9.02) * mm, "construction": true});
            skArc(sketch, "E96", {"start": v(9.72, 12.24) * mm, "mid": v(0, 15.63) * mm, "end": v(-9.72, 12.24) * mm});
            skArc(sketch, "E97", {"start": v(9.72, -12.24) * mm, "mid": v(11.36, -10.74) * mm, "end": v(12.76, -9.02) * mm, "construction": true});
            skArc(sketch, "E98", {"start": v(-9.72, -12.24) * mm, "mid": v(0, -15.63) * mm, "end": v(9.72, -12.24) * mm});
            skLineSegment(sketch, "E99", {"start": v(-9.72, 12.24) * mm, "end": v(-9.72, -12.24) * mm});
            skLineSegment(sketch, "E100", {"start": v(9.72, -12.24) * mm, "end": v(9.72, 12.24) * mm});
            skLineSegment(sketch, "E101", {"start": v(-12.76, 3.17) * mm, "end": v(-12.76, -3.17) * mm, "construction": true});
            skLineSegment(sketch, "E102", {"start": v(-9.72, 3.17) * mm, "end": v(9.72, 3.18) * mm, "construction": true});
            skPoint(sketch, "E103", {"position": v(-12.76, 0) * mm});
            skPoint(sketch, "E104", {"position": v(0, 3.18) * mm});
            skLineSegment(sketch, "E105", {"start": v(-14.33, 6.23) * mm, "end": v(-17.12, 7.44) * mm, "construction": true});
            skLineSegment(sketch, "E106", {"start": v(-12.76, 3.17) * mm, "end": v(-9.72, 3.17) * mm, "construction": true});
            skPoint(sketch, "E107", {"position": v(12.76, 0) * mm});
            skLineSegment(sketch, "E108", {"start": v(-12.76, 1.14) * mm, "end": v(-12.76, 3.17) * mm, "construction": true});
            skSolve(sketch);
        }
        {
            var Q0;
            Q0 = qSketchRegion(id + "F18", true);
            var Q1;
            Q1=makeQuery(id+"F13.opExtrude","CAP_FACE",FACE,{"disambiguationData":[OSD([sQuery(id+"F12.wireOp",EDGE,"E58")])],"isStart":true});
            extrude(context, id + "F19", {"entities" : qUnion([Q0]), "operationType" : NewBodyOperationType.REMOVE, "endBound" : BoundingType.UP_TO_SURFACE, "oppositeDirection" : true, "depth" : 25.4 * mm, "endBoundEntityFace" : qUnion([Q1]), "offsetDistance" : 25.4 * mm});
        }
        {
            var Q0;
            Q0=makeQuery(id+"F19.boolean.opBoolean","COPY",EDGE,{"derivedFrom":makeQuery(id+"F19.opExtrude","SWEPT_EDGE",EDGE,{"disambiguationData":[OSD([sQuery(id+"F18.wireOp",EDGE,"E81"),sQuery(id+"F18.wireOp",EDGE,"E90")])]})});
            var Q1;
            Q1=makeQuery(id+"F19.boolean.opBoolean","COPY",EDGE,{"derivedFrom":makeQuery(id+"F19.opExtrude","SWEPT_EDGE",EDGE,{"disambiguationData":[OSD([sQuery(id+"F18.wireOp",EDGE,"E79"),sQuery(id+"F18.wireOp",EDGE,"E87")])]})});
            var Q2;
            Q2=makeQuery(id+"F19.boolean.opBoolean","COPY",EDGE,{"derivedFrom":makeQuery(id+"F19.opExtrude","SWEPT_EDGE",EDGE,{"disambiguationData":[OSD([sQuery(id+"F18.wireOp",EDGE,"E85"),sQuery(id+"F18.wireOp",EDGE,"E94")])]})});
            var Q3;
            Q3=makeQuery(id+"F19.boolean.opBoolean","COPY",EDGE,{"derivedFrom":makeQuery(id+"F19.opExtrude","SWEPT_EDGE",EDGE,{"disambiguationData":[OSD([sQuery(id+"F18.wireOp",EDGE,"E83"),sQuery(id+"F18.wireOp",EDGE,"E91")])]})});
            var Q4;
            Q4=makeQuery(id+"F17.opExtrude","CAP_EDGE",EDGE,{"disambiguationData":[OSD([sQuery(id+"F16.wireOp",EDGE,"E74")])],"isStart":true});
            var Q5;
            Q5=makeQuery(id+"F17.opExtrude","CAP_EDGE",EDGE,{"disambiguationData":[OSD([sQuery(id+"F16.wireOp",EDGE,"E69")])],"isStart":true});
            var Q6;
            Q6=makeQuery(id+"F17.opExtrude","CAP_EDGE",EDGE,{"disambiguationData":[OSD([sQuery(id+"F16.wireOp",EDGE,"E61")])],"isStart":true});
            var Q7;
            Q7=makeQuery(id+"F17.opExtrude","CAP_EDGE",EDGE,{"disambiguationData":[OSD([sQuery(id+"F16.wireOp",EDGE,"E66")])],"isStart":true});
            fillet(context, id + "F20", {"entities" : qUnion([Q0, Q1, Q2, Q3, Q4, Q5, Q6, Q7]), "radius" : 0.5 * mm, "tangentPropagation" : true, "allowEdgeOverflow" : false});
        }
        {
            var Q0;
            Q0=makeQuery(id+"F17.opExtrude","SWEPT_EDGE",EDGE,{"disambiguationData":[OSD([sQuery(id+"F16.wireOp",EDGE,"E69"),sQuery(id+"F16.wireOp",EDGE,"E70")])]});
            var Q1;
            Q1=makeQuery(id+"F17.opExtrude","SWEPT_EDGE",EDGE,{"disambiguationData":[OSD([sQuery(id+"F16.wireOp",EDGE,"E73"),sQuery(id+"F16.wireOp",EDGE,"E74")])]});
            var Q2;
            Q2=makeQuery(id+"F17.opExtrude","SWEPT_EDGE",EDGE,{"disambiguationData":[OSD([sQuery(id+"F16.wireOp",EDGE,"E65"),sQuery(id+"F16.wireOp",EDGE,"E66")])]});
            var Q3;
            Q3=makeQuery(id+"F17.opExtrude","SWEPT_EDGE",EDGE,{"disambiguationData":[OSD([sQuery(id+"F16.wireOp",EDGE,"E61"),sQuery(id+"F16.wireOp",EDGE,"E62")])]});
            var Q4;
            Q4=makeQuery(id+"F19.boolean.opBoolean","COPY",EDGE,{"derivedFrom":makeQuery(id+"F19.opExtrude","SWEPT_EDGE",EDGE,{"disambiguationData":[OSD([sQuery(id+"F18.wireOp",EDGE,"E89"),sQuery(id+"F18.wireOp",EDGE,"E90")])]})});
            var Q5;
            Q5=makeQuery(id+"F19.boolean.opBoolean","COPY",EDGE,{"derivedFrom":makeQuery(id+"F19.opExtrude","SWEPT_EDGE",EDGE,{"disambiguationData":[OSD([sQuery(id+"F18.wireOp",EDGE,"E81"),sQuery(id+"F18.wireOp",EDGE,"E89")])]})});
            var Q6;
            Q6=makeQuery(id+"F19.boolean.opBoolean","COPY",EDGE,{"derivedFrom":makeQuery(id+"F19.opExtrude","SWEPT_EDGE",EDGE,{"disambiguationData":[OSD([sQuery(id+"F18.wireOp",EDGE,"E79"),sQuery(id+"F18.wireOp",EDGE,"E88")])]})});
            var Q7;
            Q7=makeQuery(id+"F19.boolean.opBoolean","COPY",EDGE,{"derivedFrom":makeQuery(id+"F19.opExtrude","SWEPT_EDGE",EDGE,{"disambiguationData":[OSD([sQuery(id+"F18.wireOp",EDGE,"E93"),sQuery(id+"F18.wireOp",EDGE,"E94")])]})});
            var Q8;
            Q8=makeQuery(id+"F19.boolean.opBoolean","COPY",EDGE,{"derivedFrom":makeQuery(id+"F19.opExtrude","SWEPT_EDGE",EDGE,{"disambiguationData":[OSD([sQuery(id+"F18.wireOp",EDGE,"E85"),sQuery(id+"F18.wireOp",EDGE,"E93")])]})});
            var Q9;
            Q9=makeQuery(id+"F19.boolean.opBoolean","COPY",EDGE,{"derivedFrom":makeQuery(id+"F19.opExtrude","SWEPT_EDGE",EDGE,{"disambiguationData":[OSD([sQuery(id+"F18.wireOp",EDGE,"E87"),sQuery(id+"F18.wireOp",EDGE,"E88")])]})});
            var Q10;
            Q10=makeQuery(id+"F19.boolean.opBoolean","COPY",EDGE,{"derivedFrom":makeQuery(id+"F19.opExtrude","SWEPT_EDGE",EDGE,{"disambiguationData":[OSD([sQuery(id+"F18.wireOp",EDGE,"E91"),sQuery(id+"F18.wireOp",EDGE,"E92")])]})});
            var Q11;
            Q11=makeQuery(id+"F19.boolean.opBoolean","COPY",EDGE,{"derivedFrom":makeQuery(id+"F19.opExtrude","SWEPT_EDGE",EDGE,{"disambiguationData":[OSD([sQuery(id+"F18.wireOp",EDGE,"E83"),sQuery(id+"F18.wireOp",EDGE,"E92")])]})});
            var Q12;
            Q12=makeQuery(id+"F19.boolean.opBoolean","COPY",EDGE,{"derivedFrom":makeQuery(id+"F19.opExtrude","SWEPT_EDGE",EDGE,{"disambiguationData":[OSD([sQuery(id+"F18.wireOp",EDGE,"E96"),sQuery(id+"F18.wireOp",EDGE,"E100")])]})});
            var Q13;
            Q13=makeQuery(id+"F19.boolean.opBoolean","COPY",EDGE,{"derivedFrom":makeQuery(id+"F19.opExtrude","SWEPT_EDGE",EDGE,{"disambiguationData":[OSD([sQuery(id+"F18.wireOp",EDGE,"E98"),sQuery(id+"F18.wireOp",EDGE,"E100")])]})});
            var Q14;
            Q14=makeQuery(id+"F19.boolean.opBoolean","COPY",EDGE,{"derivedFrom":makeQuery(id+"F19.opExtrude","SWEPT_EDGE",EDGE,{"disambiguationData":[OSD([sQuery(id+"F18.wireOp",EDGE,"E98"),sQuery(id+"F18.wireOp",EDGE,"E99")])]})});
            var Q15;
            Q15=makeQuery(id+"F19.boolean.opBoolean","COPY",EDGE,{"derivedFrom":makeQuery(id+"F19.opExtrude","SWEPT_EDGE",EDGE,{"disambiguationData":[OSD([sQuery(id+"F18.wireOp",EDGE,"E96"),sQuery(id+"F18.wireOp",EDGE,"E99")])]})});
            fillet(context, id + "F21", {"entities" : qUnion([Q0, Q1, Q2, Q3, Q4, Q5, Q6, Q7, Q8, Q9, Q10, Q11, Q12, Q13, Q14, Q15]), "radius" : 1.27 * mm, "tangentPropagation" : true, "allowEdgeOverflow" : false});
        }
    });
